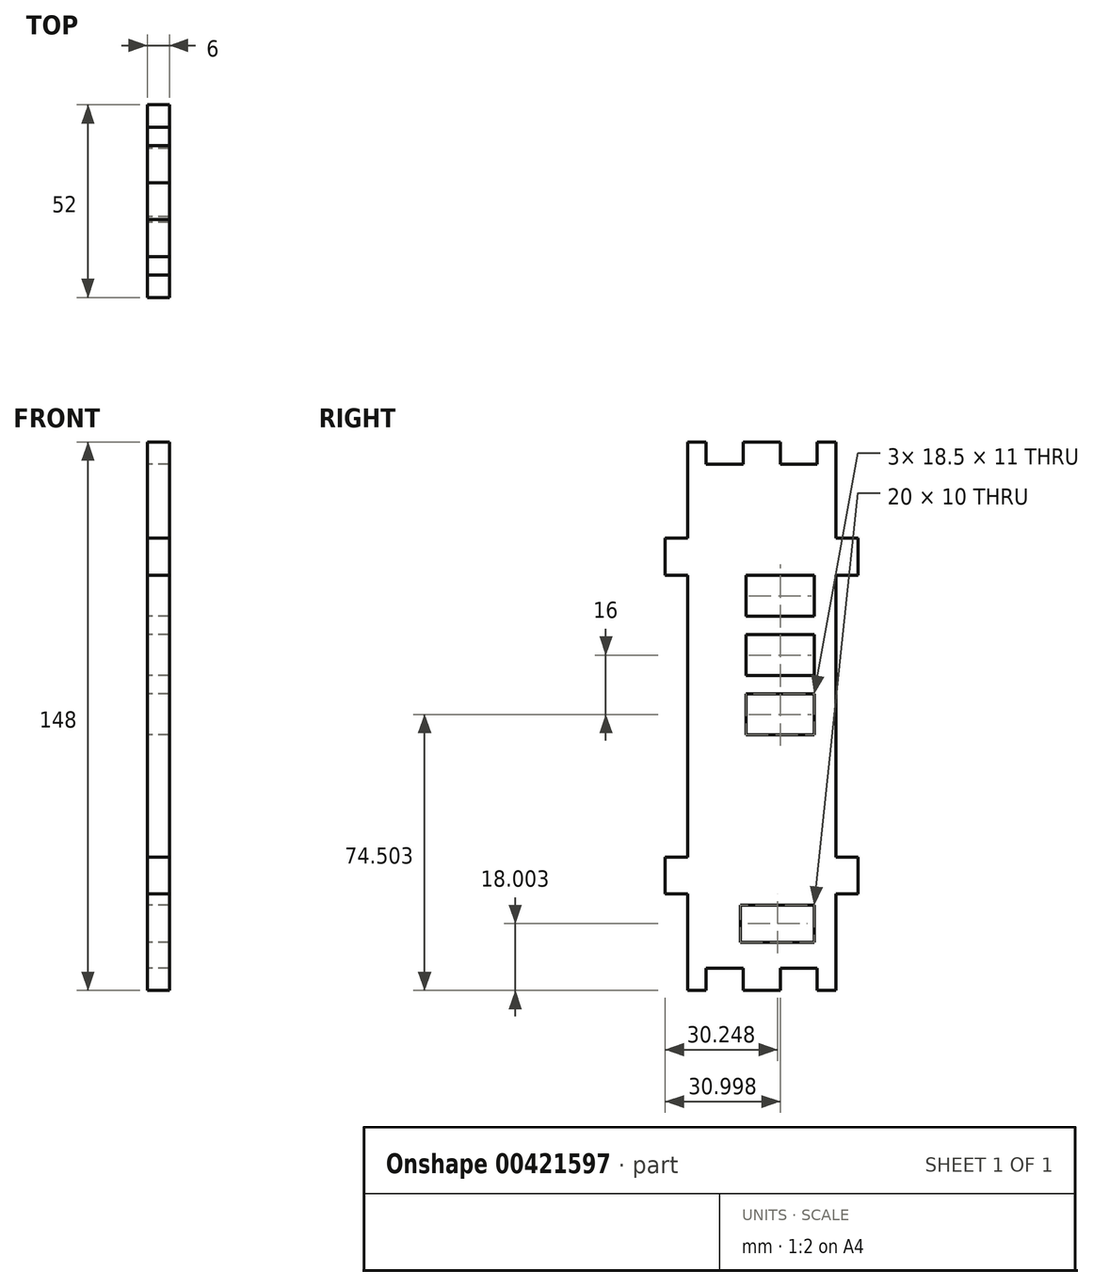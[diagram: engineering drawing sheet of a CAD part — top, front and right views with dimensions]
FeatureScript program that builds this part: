
annotation { "Feature Type Name" : "Feature", "Feature Type Description" : "" }
export const myFeature = defineFeature(function(context is Context, id is Id, definition is map)
    precondition{}
    {
        {
            var Q0;
            Q0=qCreatedBy(makeId("Right.planeOp"),FACE);
            var sketch = newSketch(context, id + "F0", { "sketchPlane" : qUnion([Q0])});
            skLineSegment(sketch, "E0.MirrorCS", {"start": v(-54.93, 42.81) * mm, "end": v(-60.93, 42.81) * mm});
            skLineSegment(sketch, "E1.MirrorCS", {"start": v(-54.93, -43.19) * mm, "end": v(-60.93, -43.19) * mm});
            skLineSegment(sketch, "E2", {"start": v(-54.93, 42.81) * mm, "end": v(-54.93, -33.19) * mm});
            skLineSegment(sketch, "E3", {"start": v(-60.93, 52.81) * mm, "end": v(-54.93, 52.81) * mm});
            skLineSegment(sketch, "E4", {"start": v(-54.93, 78.81) * mm, "end": v(-49.93, 78.81) * mm});
            skLineSegment(sketch, "E5", {"start": v(-49.93, 78.81) * mm, "end": v(-49.93, 72.81) * mm});
            skLineSegment(sketch, "E6", {"start": v(-39.93, 72.81) * mm, "end": v(-39.93, 78.81) * mm});
            skLineSegment(sketch, "E7", {"start": v(-39.93, 78.81) * mm, "end": v(-29.93, 78.81) * mm});
            skLineSegment(sketch, "E8", {"start": v(-29.93, 78.81) * mm, "end": v(-29.93, 72.81) * mm});
            skLineSegment(sketch, "E9", {"start": v(-54.93, -69.19) * mm, "end": v(-49.93, -69.19) * mm});
            skLineSegment(sketch, "E10", {"start": v(-49.93, -69.19) * mm, "end": v(-49.93, -63.19) * mm});
            skLineSegment(sketch, "E11", {"start": v(-39.93, -63.19) * mm, "end": v(-39.93, -69.19) * mm});
            skLineSegment(sketch, "E12", {"start": v(-39.93, -69.19) * mm, "end": v(-29.93, -69.19) * mm});
            skLineSegment(sketch, "E13", {"start": v(-29.93, -69.19) * mm, "end": v(-29.93, -63.19) * mm});
            skLineSegment(sketch, "E14", {"start": v(-19.93, -63.19) * mm, "end": v(-19.93, -69.19) * mm});
            skLineSegment(sketch, "E15", {"start": v(-19.93, -69.19) * mm, "end": v(-14.93, -69.19) * mm});
            skLineSegment(sketch, "E16", {"start": v(-60.93, -33.19) * mm, "end": v(-54.93, -33.19) * mm});
            skLineSegment(sketch, "E17.MirrorCS", {"start": v(-14.93, -43.19) * mm, "end": v(-8.93, -43.19) * mm});
            skLineSegment(sketch, "E18.MirrorCS", {"start": v(-8.93, -33.19) * mm, "end": v(-14.93, -33.19) * mm});
            skLineSegment(sketch, "E19.MirrorCS", {"start": v(-8.93, 52.81) * mm, "end": v(-14.93, 52.81) * mm});
            skLineSegment(sketch, "E20", {"start": v(-14.93, 78.81) * mm, "end": v(-14.93, 52.81) * mm});
            skLineSegment(sketch, "E21", {"start": v(-14.93, 42.81) * mm, "end": v(-8.93, 42.81) * mm});
            skLineSegment(sketch, "E22", {"start": v(-14.93, 42.81) * mm, "end": v(-14.93, -33.19) * mm});
            skLineSegment(sketch, "E23", {"start": v(-14.93, 78.81) * mm, "end": v(-19.93, 78.81) * mm});
            skLineSegment(sketch, "E24", {"start": v(-19.93, 78.81) * mm, "end": v(-19.93, 72.81) * mm});
            skLineSegment(sketch, "E25", {"start": v(-14.93, -43.19) * mm, "end": v(-14.93, -69.19) * mm});
            skLineSegment(sketch, "E26", {"start": v(-54.93, 52.81) * mm, "end": v(-54.93, 78.81) * mm});
            skLineSegment(sketch, "E27", {"start": v(-54.93, -43.19) * mm, "end": v(-54.93, -69.19) * mm});
            skLineSegment(sketch, "E28.bottom", {"start": v(-39.18, 31.81) * mm, "end": v(-20.68, 31.81) * mm});
            skLineSegment(sketch, "E28.top", {"start": v(-39.18, 42.81) * mm, "end": v(-20.68, 42.81) * mm});
            skLineSegment(sketch, "E28.left", {"start": v(-39.18, 31.81) * mm, "end": v(-39.18, 42.81) * mm});
            skLineSegment(sketch, "E28.right", {"start": v(-20.68, 31.81) * mm, "end": v(-20.68, 42.81) * mm});
            skLineSegment(sketch, "E29.bottom", {"start": v(-39.18, 15.81) * mm, "end": v(-20.68, 15.81) * mm});
            skLineSegment(sketch, "E29.top", {"start": v(-39.18, 26.81) * mm, "end": v(-20.68, 26.81) * mm});
            skLineSegment(sketch, "E29.left", {"start": v(-39.18, 15.81) * mm, "end": v(-39.18, 26.81) * mm});
            skLineSegment(sketch, "E29.right", {"start": v(-20.68, 15.81) * mm, "end": v(-20.68, 26.81) * mm});
            skLineSegment(sketch, "E30.bottom", {"start": v(-39.18, -0.19) * mm, "end": v(-20.68, -0.19) * mm});
            skLineSegment(sketch, "E30.top", {"start": v(-39.18, 10.81) * mm, "end": v(-20.68, 10.81) * mm});
            skLineSegment(sketch, "E30.left", {"start": v(-39.18, -0.19) * mm, "end": v(-39.18, 10.81) * mm});
            skLineSegment(sketch, "E30.right", {"start": v(-20.68, -0.19) * mm, "end": v(-20.68, 10.81) * mm});
            skLineSegment(sketch, "E31.bottom", {"start": v(-40.68, -56.19) * mm, "end": v(-20.68, -56.19) * mm});
            skLineSegment(sketch, "E31.top", {"start": v(-40.68, -46.19) * mm, "end": v(-20.68, -46.19) * mm});
            skLineSegment(sketch, "E31.left", {"start": v(-40.68, -56.19) * mm, "end": v(-40.68, -46.19) * mm});
            skLineSegment(sketch, "E31.right", {"start": v(-20.68, -56.19) * mm, "end": v(-20.68, -46.19) * mm});
            skLineSegment(sketch, "E32", {"start": v(-8.93, -33.19) * mm, "end": v(-8.93, -43.19) * mm});
            skLineSegment(sketch, "E33", {"start": v(-19.93, -63.19) * mm, "end": v(-29.93, -63.19) * mm});
            skLineSegment(sketch, "E34", {"start": v(-49.93, -63.19) * mm, "end": v(-39.93, -63.19) * mm});
            skLineSegment(sketch, "E35", {"start": v(-60.93, -33.19) * mm, "end": v(-60.93, -43.19) * mm});
            skLineSegment(sketch, "E36", {"start": v(-60.93, 52.81) * mm, "end": v(-60.93, 42.81) * mm});
            skLineSegment(sketch, "E37", {"start": v(-8.93, 52.81) * mm, "end": v(-8.93, 42.81) * mm});
            skLineSegment(sketch, "E38", {"start": v(-19.93, 72.81) * mm, "end": v(-29.93, 72.81) * mm});
            skLineSegment(sketch, "E39", {"start": v(-39.93, 72.81) * mm, "end": v(-49.93, 72.81) * mm});
            skSolve(sketch);
        }
        {
            var Q0;
            Q0=makeQuery(id+"F0.imprint","IMPRINT",FACE,{"disambiguationData":[TD([[makeQuery(id+"F0.imprint","IMPRINT",EDGE,{"derivedFrom":sQuery(id+"F0.wireOp",EDGE,"E0.MirrorCS")}),-1.0]])]});
            extrude(context, id + "F1", {"entities" : qUnion([Q0]), "depth" : 6 * mm, "offsetDistance" : 25 * mm});
        }
    });
